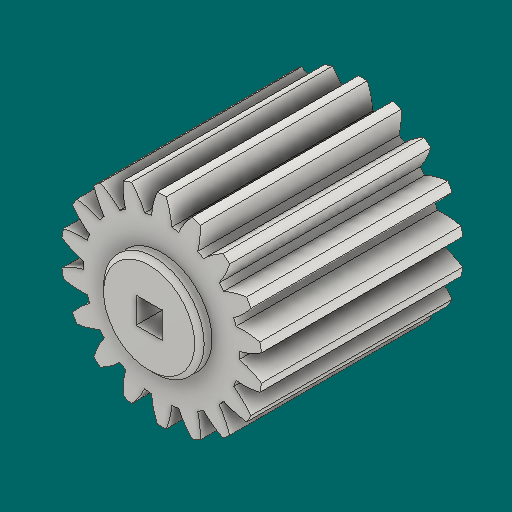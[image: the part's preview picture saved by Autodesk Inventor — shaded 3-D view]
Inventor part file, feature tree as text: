
AUTODESK INVENTOR PART (.ipt)
format: ipt  version: 2023.1 (Build 271208000, 208)  size: 361,984 bytes
history: native  units: mm (DEFAULTED — no unit token found)
features: sketch x5, extrude x4, plane x3, other x3, chamfer x2, projected_geometry x1
ambient origin geometry x8: Origin, YZ Plane, XZ Plane, XY Plane, X Axis, Y Axis, Z Axis, Center Point
bodies: Solid1 (feature_tree)
feature tree (18):
  extrude  "Extrusion1"  Depth=25.4mm TaperAngle=0.0deg
  plane  "Work Plane1"
  plane  "Work Plane2"
  plane  "Work Plane3"
  other  "Spur Gear"
  extrude  "Extrusion2"  Depth=76.2mm TaperAngle=0.0deg
  extrude  "Extrusion3"  TaperAngle=0.0deg  [1 undecoded]
  chamfer  "Chamfer1"  [1 undecoded]
  extrude  "Extrusion4"  TaperAngle=0.0deg  [1 undecoded]
  chamfer  "Chamfer2"  [1 undecoded]
  sketch  "Sketch1"  dims[d0=25.400062mm d1=25.4mm d2=0.0mm]
  sketch  "Sketch2"  dims[d3=22.86mm d4=76.2mm d5=0.0mm]
  other  "Srf1"
  sketch  "Sketch3"  dims[d6=0.0mm d7=1.745329mm d9=0.0mm]
  sketch  "Sketch4"  dims[d14=0.0mm]
  projected_geometry  "Projected Loop1"
  sketch  "Sketch5"  dims[d15=22.86mm d16=0.0mm d17=0.0mm d18=0.0mm d19=22.86mm d20=3.302mm d21=3.302mm d22=0.0mm d23=0.0mm d24=12.7mm d25=1.5875mm d26=0.0mm d27=0.6mm d28=3.175mm d29=45.0deg d30=6.604mm d31=6.604mm d32=23.8125mm d33=0.0mm d34=1.651mm d35=3.175mm d36=45.0deg]
  other  "Pitch Diameter"
note: 4 required parameter values undecoded (feature->parameter linkage not recoverable at this tier; creation-order binding heuristic only, values carry confidence <= 0.55)
